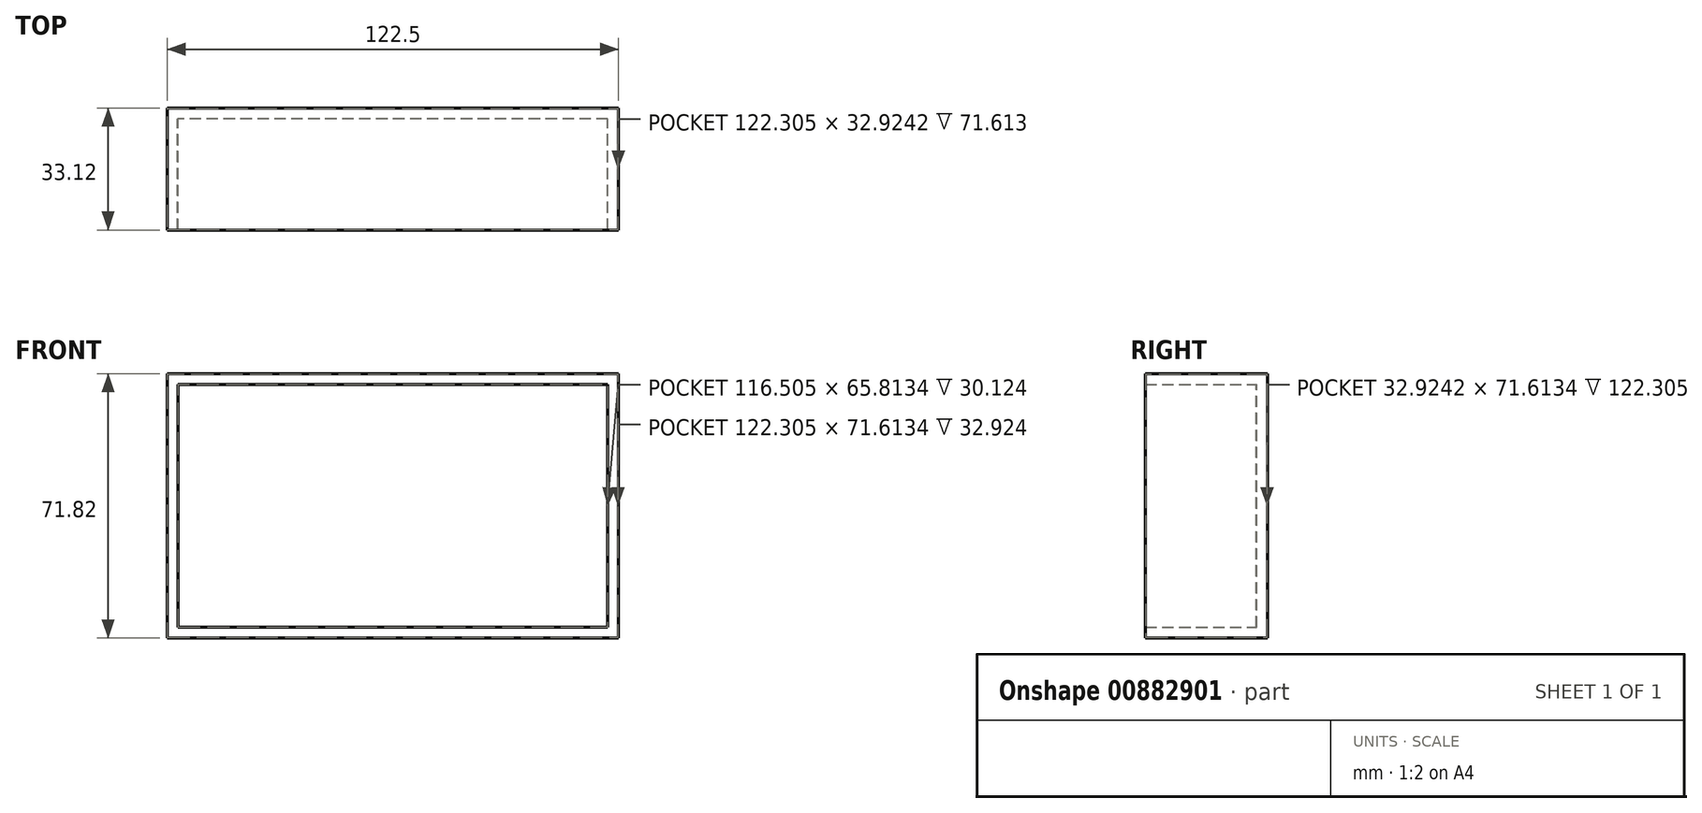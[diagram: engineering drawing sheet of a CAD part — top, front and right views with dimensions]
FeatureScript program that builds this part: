
annotation { "Feature Type Name" : "Feature", "Feature Type Description" : "" }
export const myFeature = defineFeature(function(context is Context, id is Id, definition is map)
    precondition{}
    {
        {
            var Q0;
            Q0=qCreatedBy(makeId("Front.planeOp"),FACE);
            var sketch = newSketch(context, id + "F0", { "sketchPlane" : qUnion([Q0])});
            skLineSegment(sketch, "E0.bottom", {"start": v(61.25, -35.9) * mm, "end": v(-61.25, -35.9) * mm});
            skLineSegment(sketch, "E0.top", {"start": v(61.25, 35.9) * mm, "end": v(-61.25, 35.9) * mm});
            skLineSegment(sketch, "E0.left", {"start": v(61.25, -35.9) * mm, "end": v(61.25, 35.9) * mm});
            skLineSegment(sketch, "E0.right", {"start": v(-61.25, -35.9) * mm, "end": v(-61.25, 35.9) * mm});
            skPoint(sketch, "E0.middle", {"position": v(0, 0) * mm});
            skSolve(sketch);
        }
        {
            var Q0;
            Q0 = qSketchRegion(id + "F0", true);
            extrude(context, id + "F1", {"entities" : qUnion([Q0]), "depth" : 33.12 * mm, "offsetDistance" : 25.4 * mm});
        }
        {
            var Q0;
            Q0=makeQuery(id+"F1.opExtrude","CAP_FACE",FACE,{"disambiguationData":[OSD([sQuery(id+"F0.wireOp",EDGE,"E0.bottom"),sQuery(id+"F0.wireOp",EDGE,"E0.top"),sQuery(id+"F0.wireOp",EDGE,"E0.left"),sQuery(id+"F0.wireOp",EDGE,"E0.right")])],"isStart":false});
            shell(context, id + "F2", {"entities" : qUnion([Q0]), "thickness" : 3 * mm});
        }
        {
            var Q0;
            Q0=makeQuery(id+"F2.opShell","OFFSET_FACE",FACE,{"disambiguationData":[OSD([sQuery(id+"F0.wireOp",EDGE,"E0.bottom"),sQuery(id+"F0.wireOp",EDGE,"E0.top"),sQuery(id+"F0.wireOp",EDGE,"E0.left"),sQuery(id+"F0.wireOp",EDGE,"E0.right")])]});
            var Q1;
            Q1=makeQuery(id+"F1.opExtrude","CAP_FACE",FACE,{"disambiguationData":[OSD([sQuery(id+"F0.wireOp",EDGE,"E0.bottom"),sQuery(id+"F0.wireOp",EDGE,"E0.top"),sQuery(id+"F0.wireOp",EDGE,"E0.left"),sQuery(id+"F0.wireOp",EDGE,"E0.right")])],"isStart":false});
            var Q2;
            Q2=makeQuery(id+"F1.opExtrude","SWEPT_BODY",BODY,{"disambiguationData":[OSD([sQuery(id+"F0.wireOp",EDGE,"E0.bottom"),sQuery(id+"F0.wireOp",EDGE,"E0.top"),sQuery(id+"F0.wireOp",EDGE,"E0.left"),sQuery(id+"F0.wireOp",EDGE,"E0.right")])]});
            shell(context, id + "F3", {"isHollow" : true, "entities" : qUnion([Q0, Q1]), "parts" : qUnion([Q2]), "thickness" : 0.1 * mm});
        }
    });
